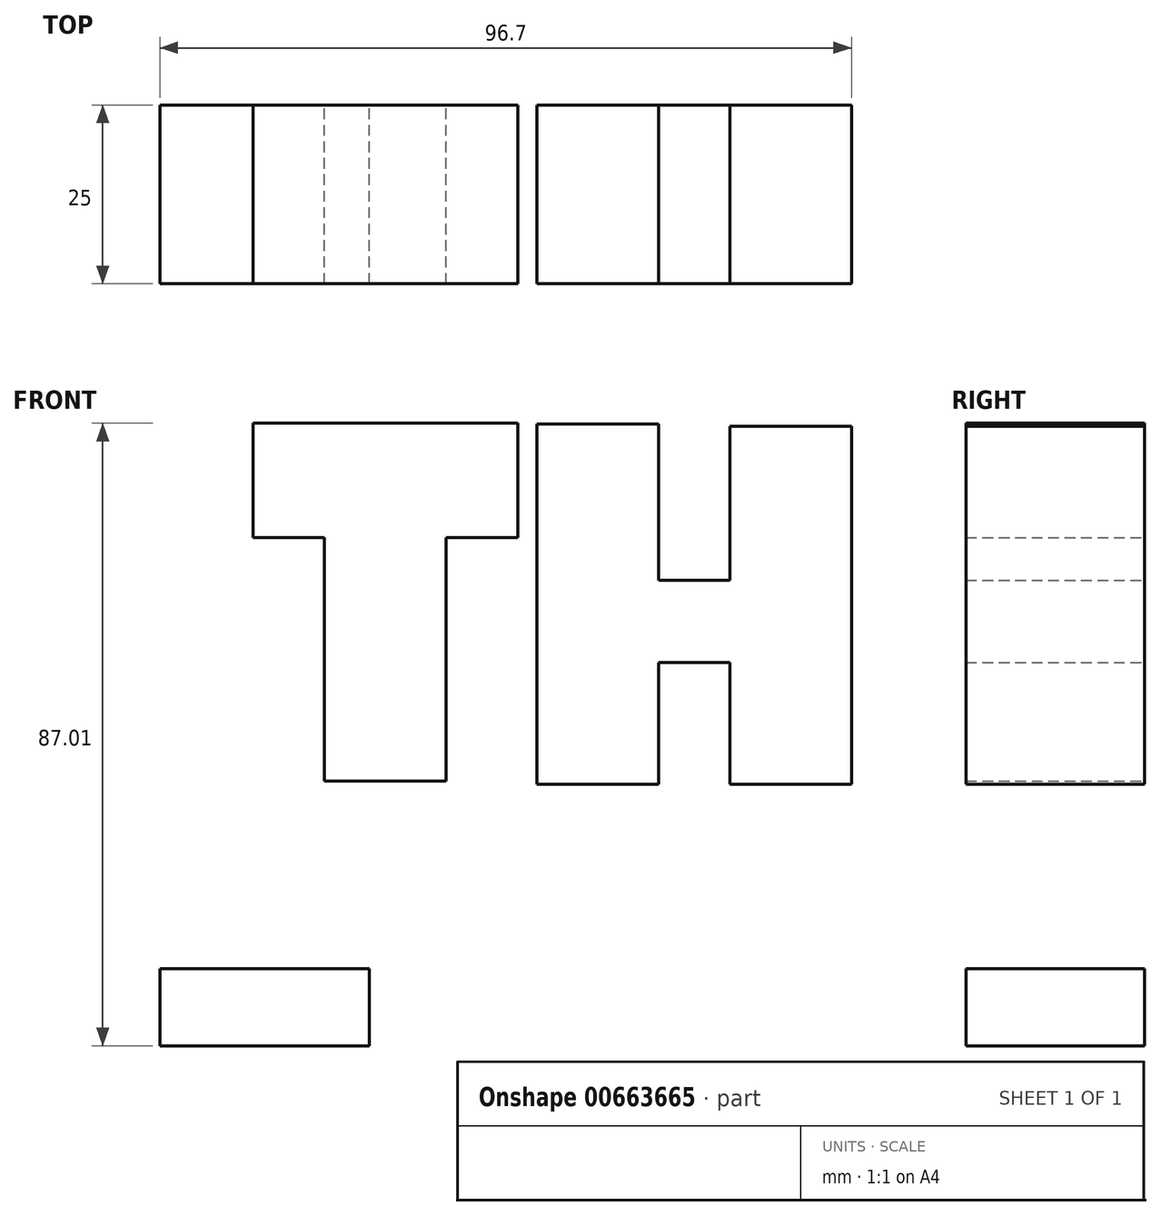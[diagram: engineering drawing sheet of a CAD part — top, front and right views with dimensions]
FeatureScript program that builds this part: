
annotation { "Feature Type Name" : "Feature", "Feature Type Description" : "" }
export const myFeature = defineFeature(function(context is Context, id is Id, definition is map)
    precondition{}
    {
        {
            var Q0;
            Q0=qCreatedBy(makeId("Front.planeOp"),FACE);
            var sketch = newSketch(context, id + "F0", { "sketchPlane" : qUnion([Q0])});
            skLineSegment(sketch, "E0.bottom", {"start": v(-18.5, 52) * mm, "end": v(18.5, 52) * mm});
            skLineSegment(sketch, "E0.top", {"start": v(-18.5, 36) * mm, "end": v(-8.5, 36) * mm});
            skLineSegment(sketch, "E0.left", {"start": v(-18.5, 52) * mm, "end": v(-18.5, 36) * mm});
            skLineSegment(sketch, "E0.right", {"start": v(18.5, 52) * mm, "end": v(18.5, 36) * mm});
            skLineSegment(sketch, "E1.top", {"start": v(-8.5, 2) * mm, "end": v(8.5, 2) * mm});
            skLineSegment(sketch, "E1.left", {"start": v(-8.5, 36) * mm, "end": v(-8.5, 2) * mm});
            skLineSegment(sketch, "E1.right", {"start": v(8.5, 36) * mm, "end": v(8.5, 2) * mm});
            skLineSegment(sketch, "E2.trimOffspring", {"start": v(8.5, 36) * mm, "end": v(18.5, 36) * mm});
            skLineSegment(sketch, "E3.left", {"start": v(-18.5, 36) * mm, "end": v(-18.5, 36) * mm});
            skLineSegment(sketch, "E3.right", {"start": v(18.5, 36) * mm, "end": v(18.5, 36) * mm});
            skLineSegment(sketch, "E4.bottom", {"start": v(38.18, 51.91) * mm, "end": v(21.18, 51.91) * mm});
            skLineSegment(sketch, "E4.top", {"start": v(38.18, 1.56) * mm, "end": v(21.18, 1.56) * mm});
            skLineSegment(sketch, "E4.left", {"start": v(38.18, 51.91) * mm, "end": v(38.18, 30.06) * mm});
            skLineSegment(sketch, "E4.right", {"start": v(21.18, 51.91) * mm, "end": v(21.18, 1.56) * mm});
            skLineSegment(sketch, "E5.bottom", {"start": v(38.18, 30.06) * mm, "end": v(48.18, 30.06) * mm});
            skLineSegment(sketch, "E5.top", {"start": v(38.18, 18.54) * mm, "end": v(48.18, 18.54) * mm});
            skLineSegment(sketch, "E6.bottom", {"start": v(48.18, 1.56) * mm, "end": v(65.18, 1.56) * mm});
            skLineSegment(sketch, "E6.top", {"start": v(48.18, 51.56) * mm, "end": v(65.18, 51.56) * mm});
            skLineSegment(sketch, "E6.left", {"start": v(48.18, 1.56) * mm, "end": v(48.18, 18.54) * mm});
            skLineSegment(sketch, "E6.right", {"start": v(65.18, 1.56) * mm, "end": v(65.18, 51.56) * mm});
            skLineSegment(sketch, "E7.trimOffspring", {"start": v(38.18, 18.54) * mm, "end": v(38.18, 1.56) * mm});
            skLineSegment(sketch, "E8.trimOffspring", {"start": v(48.18, 30.06) * mm, "end": v(48.18, 51.56) * mm});
            skLineSegment(sketch, "E9.bottom", {"start": v(-31.52, -24.27) * mm, "end": v(-2.25, -24.27) * mm});
            skLineSegment(sketch, "E9.top", {"start": v(-31.52, -35) * mm, "end": v(-2.25, -35) * mm});
            skLineSegment(sketch, "E9.left", {"start": v(-31.52, -24.27) * mm, "end": v(-31.52, -35) * mm});
            skLineSegment(sketch, "E9.right", {"start": v(-2.25, -24.27) * mm, "end": v(-2.25, -35) * mm});
            skSolve(sketch);
        }
        {
            var Q0;
            Q0 = qSketchRegion(id + "F0", true);
            extrude(context, id + "F1", {"entities" : qUnion([Q0]), "depth" : 25 * mm, "offsetDistance" : 25 * mm});
        }
    });
